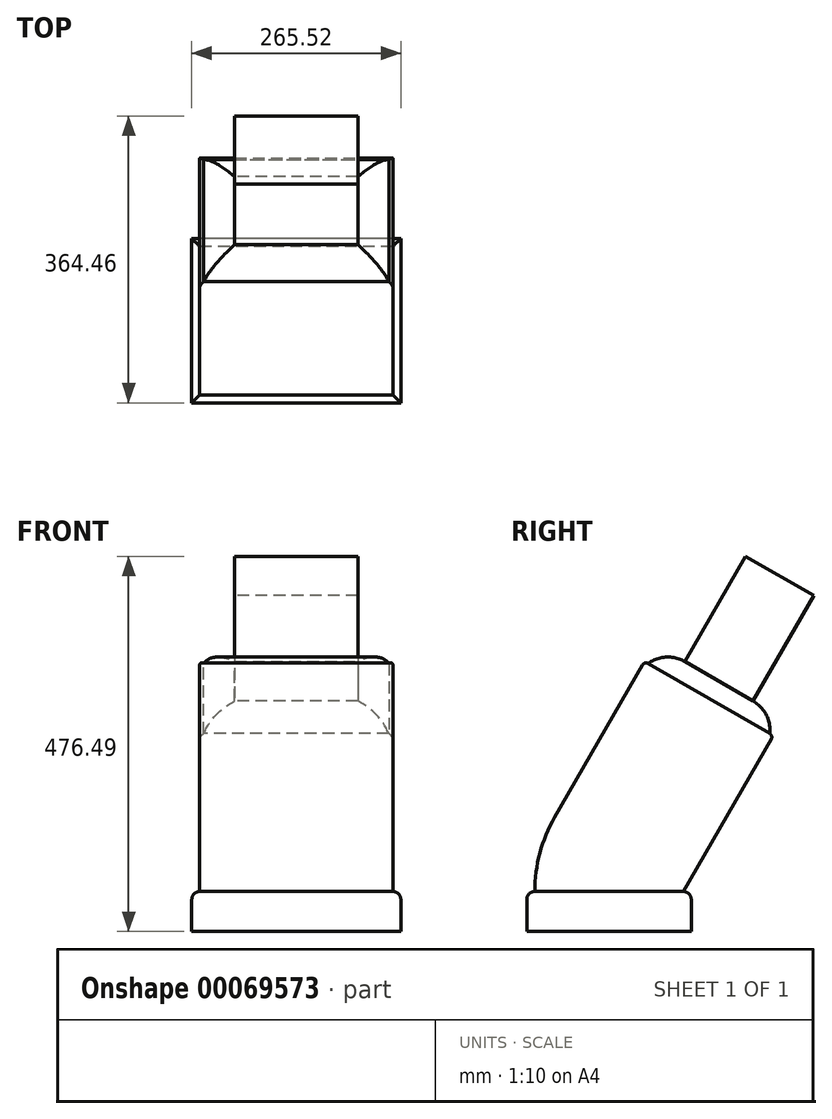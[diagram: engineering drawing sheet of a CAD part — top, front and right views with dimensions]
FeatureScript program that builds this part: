
annotation { "Feature Type Name" : "Feature", "Feature Type Description" : "" }
export const myFeature = defineFeature(function(context is Context, id is Id, definition is map)
    precondition{}
    {
        {
            var Q0;
            Q0=qCreatedBy(makeId("Top.planeOp"),FACE);
            var sketch = newSketch(context, id + "F0", { "sketchPlane" : qUnion([Q0])});
            skLineSegment(sketch, "E0.rect.bottom", {"start": v(132.76, -104.47) * mm, "end": v(-132.76, -104.47) * mm});
            skLineSegment(sketch, "E0.rect.top", {"start": v(132.76, 104.47) * mm, "end": v(-132.76, 104.47) * mm});
            skLineSegment(sketch, "E0.rect.left", {"start": v(132.76, -104.47) * mm, "end": v(132.76, 104.47) * mm});
            skLineSegment(sketch, "E0.rect.right", {"start": v(-132.76, -104.47) * mm, "end": v(-132.76, 104.47) * mm});
            skPoint(sketch, "E0.rect.middle", {"position": v(0, 0) * mm});
            skSolve(sketch);
        }
        {
            var Q0;
            Q0=makeQuery(id+"F0.imprint","IMPRINT",FACE,{"disambiguationData":[TD([[makeQuery(id+"F0.imprint","IMPRINT",EDGE,{"derivedFrom":sQuery(id+"F0.wireOp",EDGE,"E0.rect.bottom")}),-1.0]])]});
            extrude(context, id + "F1", {"entities" : qUnion([Q0]), "depth" : 50.8 * mm});
        }
        {
            var Q0;
            Q0=makeQuery(id+"F1.opExtrude","CAP_EDGE",EDGE,{"disambiguationData":[OSD([sQuery(id+"F0.wireOp",EDGE,"E0.rect.right")])],"isStart":false});
            var Q1;
            Q1=makeQuery(id+"F1.opExtrude","CAP_EDGE",EDGE,{"disambiguationData":[OSD([sQuery(id+"F0.wireOp",EDGE,"E0.rect.bottom")])],"isStart":false});
            var Q2;
            Q2=makeQuery(id+"F1.opExtrude","CAP_EDGE",EDGE,{"disambiguationData":[OSD([sQuery(id+"F0.wireOp",EDGE,"E0.rect.left")])],"isStart":false});
            var Q3;
            Q3=makeQuery(id+"F1.opExtrude","CAP_EDGE",EDGE,{"disambiguationData":[OSD([sQuery(id+"F0.wireOp",EDGE,"E0.rect.top")])],"isStart":false});
            fillet(context, id + "F2", {"entities" : qUnion([Q0, Q1, Q2, Q3]), "radius" : 10.16 * mm, "tangentPropagation" : true, "allowEdgeOverflow" : false});
        }
        {
            var Q0;
            Q0=makeQuery(id+"F1.opExtrude","CAP_FACE",FACE,{"disambiguationData":[OSD([sQuery(id+"F0.wireOp",EDGE,"E0.rect.bottom"),sQuery(id+"F0.wireOp",EDGE,"E0.rect.top"),sQuery(id+"F0.wireOp",EDGE,"E0.rect.left"),sQuery(id+"F0.wireOp",EDGE,"E0.rect.right")])],"isStart":false});
            extrude(context, id + "F3", {"entities" : qUnion([Q0]), "operationType" : NewBodyOperationType.ADD, "oppositeDirection" : true, "depth" : 18.97 * mm});
        }
        {
            var Q0;
            Q0=makeQuery(id+"F1.opExtrude","CAP_FACE",FACE,{"disambiguationData":[OSD([sQuery(id+"F0.wireOp",EDGE,"E0.rect.bottom"),sQuery(id+"F0.wireOp",EDGE,"E0.rect.top"),sQuery(id+"F0.wireOp",EDGE,"E0.rect.left"),sQuery(id+"F0.wireOp",EDGE,"E0.rect.right")])],"isStart":false});
            var Q1;
            {var subQ0=sQuery(id+"F0.wireOp",EDGE,"E0.rect.top");Q1=makeQuery(id+"F2.opFillet","BLEND_EDGE",EDGE,{"blendedFrom":[makeQuery(id+"F1.opExtrude","CAP_EDGE",EDGE,{"disambiguationData":[OSD([subQ0])],"isStart":false}),makeQuery(id+"F1.opExtrude","CAP_FACE",FACE,{"disambiguationData":[OSD([sQuery(id+"F0.wireOp",EDGE,"E0.rect.bottom"),subQ0,sQuery(id+"F0.wireOp",EDGE,"E0.rect.left"),sQuery(id+"F0.wireOp",EDGE,"E0.rect.right")])],"isStart":false})],"blendedInto":[makeQuery(id+"F1.opExtrude","CAP_FACE",FACE,{"disambiguationData":[OSD([sQuery(id+"F0.wireOp",EDGE,"E0.rect.bottom"),subQ0,sQuery(id+"F0.wireOp",EDGE,"E0.rect.left"),sQuery(id+"F0.wireOp",EDGE,"E0.rect.right")])],"isStart":false})]});}
            revolve(context, id + "F4", {"operationType" : NewBodyOperationType.ADD, "entities" : qUnion([Q0]), "axis" : qUnion([Q1]), "revolveType" : RevolveType.ONE_DIRECTION, "angle" : 30 * degree});
        }
        {
            var Q0;
            Q0=makeQuery(id+"F4.opRevolve","CAP_FACE",FACE,{"disambiguationData":[OSD([sQuery(id+"F0.wireOp",EDGE,"E0.rect.bottom"),sQuery(id+"F0.wireOp",EDGE,"E0.rect.top"),sQuery(id+"F0.wireOp",EDGE,"E0.rect.left"),sQuery(id+"F0.wireOp",EDGE,"E0.rect.right")])],"isStart":false});
            extrude(context, id + "F5", {"entities" : qUnion([Q0]), "operationType" : NewBodyOperationType.ADD, "depth" : 228.6 * mm});
        }
        {
            var Q0;
            Q0=makeQuery(id+"F5.opExtrude","CAP_FACE",FACE,{"disambiguationData":[OSD([sQuery(id+"F0.wireOp",EDGE,"E0.rect.bottom"),sQuery(id+"F0.wireOp",EDGE,"E0.rect.top"),sQuery(id+"F0.wireOp",EDGE,"E0.rect.left"),sQuery(id+"F0.wireOp",EDGE,"E0.rect.right")])],"isStart":false});
            fillet(context, id + "F6", {"entities" : qUnion([Q0]), "radius" : 5.08 * mm, "tangentPropagation" : true, "allowEdgeOverflow" : false});
        }
        {
            var Q0;
            Q0=makeQuery(id+"F5.opExtrude","CAP_FACE",FACE,{"disambiguationData":[OSD([sQuery(id+"F0.wireOp",EDGE,"E0.rect.bottom"),sQuery(id+"F0.wireOp",EDGE,"E0.rect.top"),sQuery(id+"F0.wireOp",EDGE,"E0.rect.left"),sQuery(id+"F0.wireOp",EDGE,"E0.rect.right")])],"isStart":false});
            extrude(context, id + "F7", {"entities" : qUnion([Q0]), "operationType" : NewBodyOperationType.ADD, "depth" : 25.4 * mm});
        }
        {
            var Q0;
            Q0=makeQuery(id+"F7.opExtrude","CAP_FACE",FACE,{"disambiguationData":[OSD([sQuery(id+"F0.wireOp",EDGE,"E0.rect.bottom"),sQuery(id+"F0.wireOp",EDGE,"E0.rect.top"),sQuery(id+"F0.wireOp",EDGE,"E0.rect.left"),sQuery(id+"F0.wireOp",EDGE,"E0.rect.right")])],"isStart":false});
            fillet(context, id + "F8", {"entities" : qUnion([Q0]), "radius" : 43.15 * mm, "tangentPropagation" : true, "allowEdgeOverflow" : false});
        }
        {
            var Q0;
            Q0=makeQuery(id+"F7.opExtrude","CAP_FACE",FACE,{"disambiguationData":[OSD([sQuery(id+"F0.wireOp",EDGE,"E0.rect.bottom"),sQuery(id+"F0.wireOp",EDGE,"E0.rect.top"),sQuery(id+"F0.wireOp",EDGE,"E0.rect.left"),sQuery(id+"F0.wireOp",EDGE,"E0.rect.right")])],"isStart":false});
            extrude(context, id + "F9", {"entities" : qUnion([Q0]), "operationType" : NewBodyOperationType.ADD, "depth" : 154.29 * mm});
        }
    });
